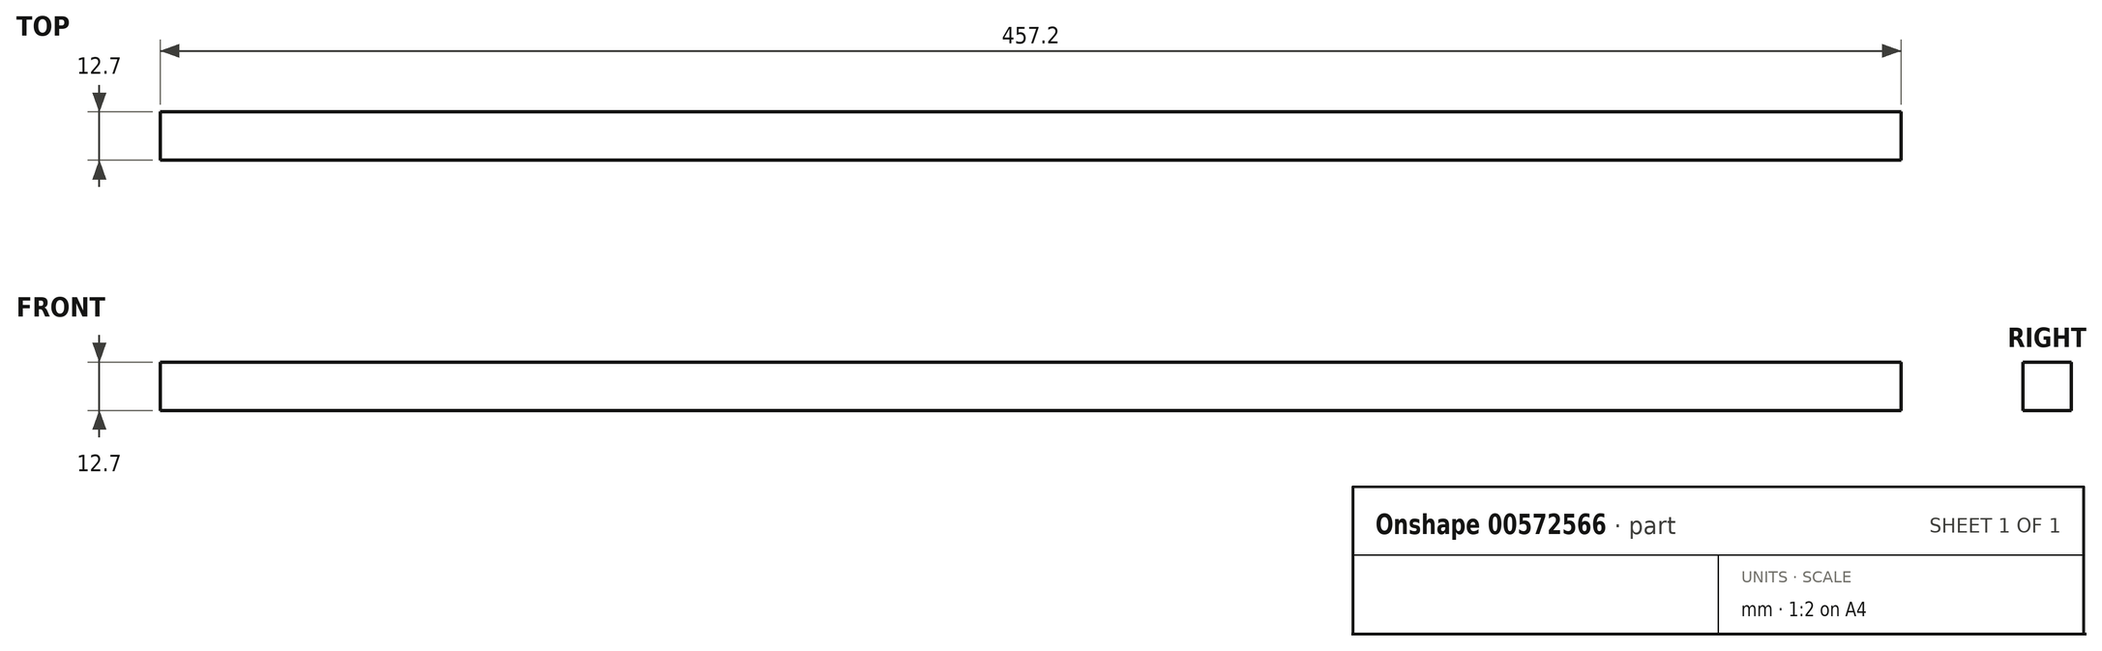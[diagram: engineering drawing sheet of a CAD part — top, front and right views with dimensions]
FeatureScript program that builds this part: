
annotation { "Feature Type Name" : "Feature", "Feature Type Description" : "" }
export const myFeature = defineFeature(function(context is Context, id is Id, definition is map)
    precondition{}
    {
        {
            var Q0;
            Q0=qCreatedBy(makeId("Front.planeOp"),FACE);
            var sketch = newSketch(context, id + "F0", { "sketchPlane" : qUnion([Q0])});
            skLineSegment(sketch, "E0.bottom", {"start": v(-211.92, -89.49) * mm, "end": v(245.28, -89.49) * mm});
            skLineSegment(sketch, "E0.top", {"start": v(-211.92, -102.19) * mm, "end": v(245.28, -102.19) * mm});
            skLineSegment(sketch, "E0.left", {"start": v(-211.92, -89.49) * mm, "end": v(-211.92, -102.19) * mm});
            skLineSegment(sketch, "E0.right", {"start": v(245.28, -89.49) * mm, "end": v(245.28, -102.19) * mm});
            skSolve(sketch);
        }
        {
            var Q0;
            Q0=makeQuery(id+"F0.imprint","IMPRINT",FACE,{"disambiguationData":[TD([[makeQuery(id+"F0.imprint","IMPRINT",EDGE,{"derivedFrom":sQuery(id+"F0.wireOp",EDGE,"E0.bottom")}),-1.0]])]});
            extrude(context, id + "F1", {"entities" : qUnion([Q0]), "depth" : 12.7 * mm, "offsetDistance" : 25.4 * mm});
        }
    });
